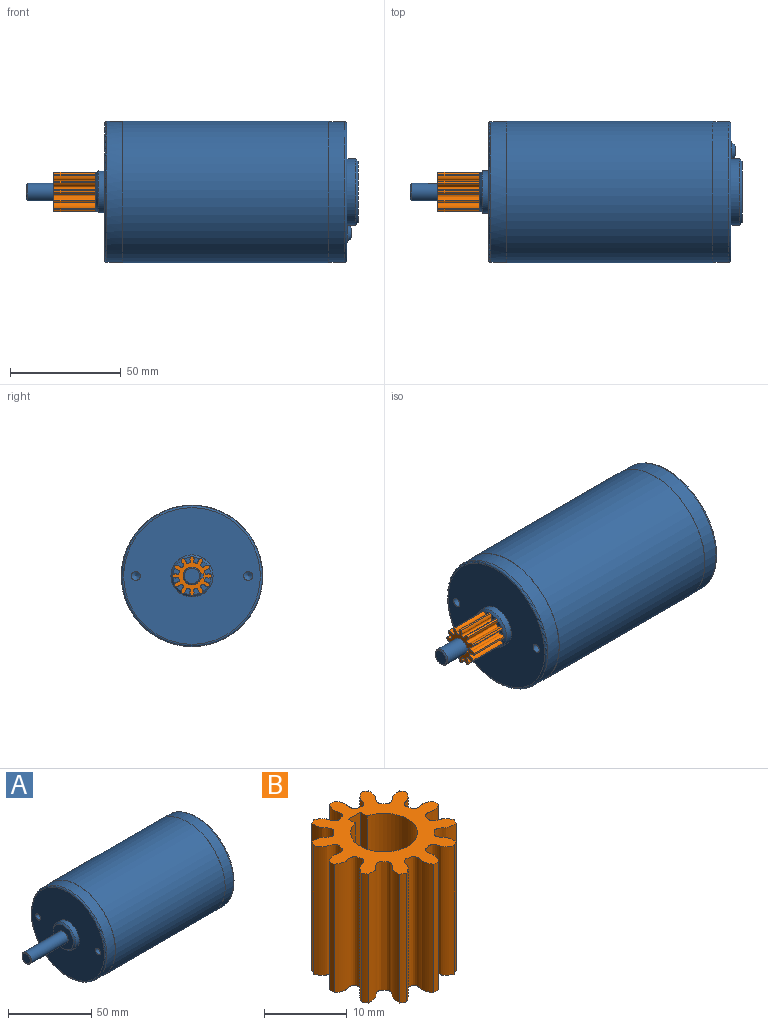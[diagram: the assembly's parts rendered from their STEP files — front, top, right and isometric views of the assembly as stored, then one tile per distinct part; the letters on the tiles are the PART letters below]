
ASSEMBLY  parts=2 mates=1
PART A: 33 faces, bbox 150.2x69x69 mm
  f0: cone r=4mm half-angle=45deg, axis (1,0,0), area 16.7mm2, adj f18,f22
  f1: cone r=9.53mm half-angle=45deg, axis (1,0,0), area 81.4mm2, adj f13,f27
  f2: cone r=14.02mm half-angle=45deg, axis (-1,0,0), area 131.2mm2, adj f17,f23
  f3: cone r=2.12mm half-angle=45deg, axis (-1,0,0), area 62.9mm2, adj f5,f29
  f4: cone r=2.12mm half-angle=45deg, axis (-1,0,0), area 62.9mm2, adj f6,f28
  f5: cylinder r=4.32mm len=8.64mm, axis (-1,0,0), area 1.3mm2, adj f3,f21
  f6: cylinder r=4.32mm len=8.64mm, axis (-1,0,0), area 1.3mm2, adj f4,f21
  f7: cone r=2.02mm half-angle=59deg, axis (-1,0,0), area 14.9mm2, adj f8
  f8: cylinder r=2.02mm len=13.61mm, axis (-1,0,0), area 172.7mm2, adj f7,f26
  f9: cone r=2.02mm half-angle=59deg, axis (-1,0,0), area 14.9mm2, adj f10
  f10: cylinder r=2.02mm len=13.61mm, axis (-1,0,0), area 172.7mm2, adj f9,f26
  f11: torus R=30.88mm, axis (1,0,0), area 311mm2, adj f16,f21
  f12: torus R=30.88mm, axis (-1,0,0), area 311mm2, adj f14,f26
  f13: cylinder r=9.53mm len=19.05mm, axis (1,0,0), area 178.6mm2, adj f1,f26
  f14: cylinder r=31.88mm len=63.75mm, axis (1,0,0), area 1448mm2, adj f12,f25
  f15: cylinder r=32mm len=93.14mm, axis (1,0,0), area 18729.4mm2, adj f24,f25
  f16: cylinder r=31.88mm len=63.75mm, axis (1,0,0), area 1448mm2, adj f11,f24
  f17: cylinder r=15.04mm len=30.07mm, axis (1,0,0), area 376.4mm2, adj f2,f21
  f18: cylinder r=4mm len=31.1mm, axis (1,0,0), area 739mm2, adj f0,f19,f20,f27,f31,f32
  f19: cylinder r=1mm len=2mm, axis (0,1,0), area 3.4mm2, adj f18,f30,f31,f32
  f20: cylinder r=1mm len=2mm, axis (0,-1,0), area 3.4mm2, adj f18,f30,f31,f32
  f21: plane 61.75x61.75mm, normal (1,0,0), area 2167.7mm2, adj f5,f6,f11,f17
  f22: plane 7x7mm, normal (-1,0,0), area 38.5mm2, adj f0
  f23: plane 28.04x28.04mm, normal (1,0,0), area 617.6mm2, adj f2
  f24: plane 64.01x64.01mm, normal (1,0,0), area 25.5mm2, adj f15,f16
  f25: plane 64.01x64.01mm, normal (-1,0,0), area 25.5mm2, adj f14,f15
  f26: plane 61.75x61.75mm, normal (-1,0,0), area 2684.5mm2, adj f8,f10,f12,f13
  f27: plane 17.02x17.02mm, normal (-1,0,0), area 177.2mm2, adj f1,f18
  f28: plane 4.24x4.24mm, normal (1,0,0), area 14.1mm2, adj f4
  f29: plane 4.24x4.24mm, normal (1,0,0), area 14.1mm2, adj f3
  f30: plane 21.5x2mm, normal (0,1,0), area 42.1mm2, adj f19,f20,f31,f32
  f31: plane 19.5x1.07mm, normal (0,0,1), area 20.9mm2, adj f18,f19,f20,f30
  f32: plane 19.5x1.07mm, normal (0,0,-1), area 20.9mm2, adj f18,f19,f20,f30
PART B: 30 faces, bbox 18x18x19.2 mm
  f0: cylinder r=4.03mm len=19mm, axis (0,0,-1), area 441.1mm2, adj f2,f26,f27,f28
  f1: cylinder r=8.89mm len=19mm, axis (0,0,1), area 17.2mm2, adj f2,f14,f15,f26
  f2: plane 17.95x17.95mm, normal (0,0,1), area 120.6mm2, adj f0,f1,f3,f4,f5,f6,f7,f8
  f3: cylinder r=8.89mm len=19mm, axis (0,0,1), area 17.2mm2, adj f2,f24,f25,f26
  f4: cylinder r=8.89mm len=19mm, axis (0,0,1), area 17.2mm2, adj f2,f14,f25,f26
  f5: cylinder r=8.89mm len=19mm, axis (0,0,1), area 17.2mm2, adj f2,f23,f24,f26
  f6: cylinder r=8.89mm len=19mm, axis (0,0,1), area 17.2mm2, adj f2,f22,f23,f26
  f7: cylinder r=8.89mm len=19mm, axis (0,0,1), area 17.2mm2, adj f2,f21,f22,f26
  f8: cylinder r=8.89mm len=19mm, axis (0,0,1), area 17.2mm2, adj f2,f20,f21,f26
  f9: cylinder r=8.89mm len=19mm, axis (0,0,1), area 17.2mm2, adj f2,f19,f20,f26
  f10: cylinder r=8.89mm len=19mm, axis (0,0,1), area 17.2mm2, adj f2,f18,f19,f26
  f11: cylinder r=8.89mm len=19mm, axis (0,0,1), area 17.2mm2, adj f2,f17,f18,f26
  f12: cylinder r=8.89mm len=19mm, axis (0,0,1), area 17.2mm2, adj f2,f16,f17,f26
  f13: cylinder r=8.89mm len=19mm, axis (0,0,1), area 17.2mm2, adj f2,f15,f16,f26
  f14: extruded ~19x3.59mm, area 135.8mm2, adj f1,f2,f4,f26
  f15: extruded ~19x3.59mm, area 135.8mm2, adj f1,f2,f13,f26
  f16: extruded ~19x3.56mm, area 135.8mm2, adj f2,f12,f13,f26
  f17: extruded ~19x3.59mm, area 135.8mm2, adj f2,f11,f12,f26
  f18: extruded ~19x3.59mm, area 135.8mm2, adj f2,f10,f11,f26
  f19: extruded ~19x3.56mm, area 135.8mm2, adj f2,f9,f10,f26
  f20: extruded ~19x3.59mm, area 135.8mm2, adj f2,f8,f9,f26
  f21: extruded ~19x3.59mm, area 135.8mm2, adj f2,f7,f8,f26
  f22: extruded ~19x3.56mm, area 135.8mm2, adj f2,f6,f7,f26
  f23: extruded ~19x3.59mm, area 135.8mm2, adj f2,f5,f6,f26
  f24: extruded ~19x3.59mm, area 135.8mm2, adj f2,f3,f5,f26
  f25: extruded ~19x3.56mm, area 135.8mm2, adj f2,f3,f4,f26
  f26: plane 17.95x17.95mm, normal (0,0,-1), area 118.5mm2, adj f0,f1,f3,f4,f5,f6,f7,f8
  f27: plane 19x1.13mm, normal (1,0,0), area 21.5mm2, adj f0,f2,f26,f29
  f28: plane 19x1.13mm, normal (-1,0,0), area 21.5mm2, adj f0,f2,f26,f29
  f29: plane 19x2.05mm, normal (0,-1,0), area 39mm2, adj f2,f26,f27,f28
PLACE A t=(-44.06,-7.12,-6.72)mm
PLACE B rot(axis=(0.71,0,-0.71),180deg) t=(-57.56,-7.12,-6.72)mm
MATE fastened B.f0 <-> A.f0  axis (1,0,0) through (-48.06,-7.12,-6.72)mm
